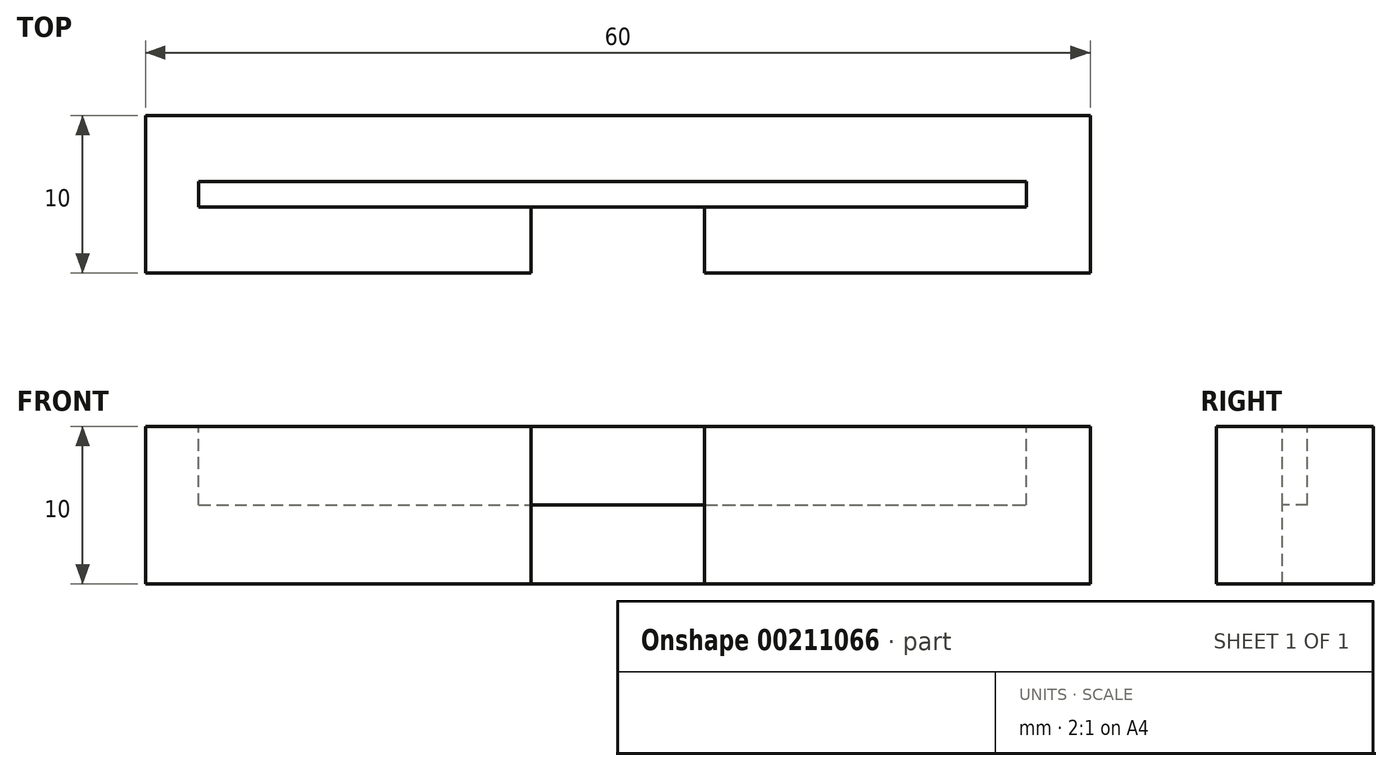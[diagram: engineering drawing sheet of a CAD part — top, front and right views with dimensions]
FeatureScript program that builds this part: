
annotation { "Feature Type Name" : "Feature", "Feature Type Description" : "" }
export const myFeature = defineFeature(function(context is Context, id is Id, definition is map)
    precondition{}
    {
        {
            var Q0;
            Q0=qCreatedBy(makeId("Front.planeOp"),FACE);
            var sketch = newSketch(context, id + "F0", { "sketchPlane" : qUnion([Q0])});
            skLineSegment(sketch, "E0.bottom", {"start": v(-24.64, -11.96) * mm, "end": v(35.36, -11.96) * mm});
            skLineSegment(sketch, "E0.top", {"start": v(-24.64, -21.96) * mm, "end": v(35.36, -21.96) * mm});
            skLineSegment(sketch, "E0.left", {"start": v(-24.64, -11.96) * mm, "end": v(-24.64, -21.96) * mm});
            skLineSegment(sketch, "E0.right", {"start": v(35.36, -11.96) * mm, "end": v(35.36, -21.96) * mm});
            skSolve(sketch);
        }
        {
            var Q0;
            Q0 = qSketchRegion(id + "F0", true);
            extrude(context, id + "F1", {"entities" : qUnion([Q0]), "depth" : 10 * mm});
        }
        {
            var Q0;
            Q0=makeQuery(id+"F1.opExtrude","SWEPT_FACE",FACE,{"disambiguationData":[OSD([sQuery(id+"F0.wireOp",EDGE,"E0.bottom")])]});
            var sketch = newSketch(context, id + "F2", { "sketchPlane" : qUnion([Q0])});
            skLineSegment(sketch, "E1.bottom", {"start": v(-21.26, -4.2) * mm, "end": v(31.31, -4.2) * mm});
            skLineSegment(sketch, "E1.top", {"start": v(-21.26, -5.8) * mm, "end": v(31.31, -5.8) * mm});
            skLineSegment(sketch, "E1.left", {"start": v(-21.26, -4.2) * mm, "end": v(-21.26, -5.8) * mm});
            skLineSegment(sketch, "E1.right", {"start": v(31.31, -4.2) * mm, "end": v(31.31, -5.8) * mm});
            skSolve(sketch);
        }
        {
            var Q0;
            Q0 = qSketchRegion(id + "F2", true);
            extrude(context, id + "F3", {"entities" : qUnion([Q0]), "operationType" : NewBodyOperationType.REMOVE, "oppositeDirection" : true, "depth" : 5 * mm});
        }
        {
            var Q0;
            {var subQ2=sQuery(id+"F0.wireOp",EDGE,"E0.bottom");Q0=makeQuery(id+"F3.boolean.opBoolean","SPLIT",FACE,{"disambiguationData":[TD([makeQuery(id+"F3.opExtrude","SWEPT_FACE",FACE,{"disambiguationData":[OSD([sQuery(id+"F2.wireOp",EDGE,"E1.top")])]})])],"derivedFrom":makeQuery(id+"F1.opExtrude","SWEPT_FACE",FACE,{"disambiguationData":[OSD([subQ2])]})});}
            var sketch = newSketch(context, id + "F4", { "sketchPlane" : qUnion([Q0])});
            skLineSegment(sketch, "E2.bottom", {"start": v(-0.14, -5.8) * mm, "end": v(10.86, -5.8) * mm});
            skLineSegment(sketch, "E2.top", {"start": v(-0.14, -10) * mm, "end": v(10.86, -10) * mm});
            skLineSegment(sketch, "E2.left", {"start": v(-0.14, -5.8) * mm, "end": v(-0.14, -10) * mm});
            skLineSegment(sketch, "E2.right", {"start": v(10.86, -5.8) * mm, "end": v(10.86, -10) * mm});
            skLineSegment(sketch, "E3", {"start": v(-24.64, -10) * mm, "end": v(-0.14, -10) * mm, "construction": true});
            skLineSegment(sketch, "E4", {"start": v(10.86, -10) * mm, "end": v(35.36, -10) * mm, "construction": true});
            skSolve(sketch);
        }
        {
            var Q0;
            Q0 = qSketchRegion(id + "F4", true);
            extrude(context, id + "F5", {"entities" : qUnion([Q0]), "operationType" : NewBodyOperationType.REMOVE, "endBound" : BoundingType.THROUGH_ALL, "oppositeDirection" : true, "depth" : 25 * mm});
        }
    });
